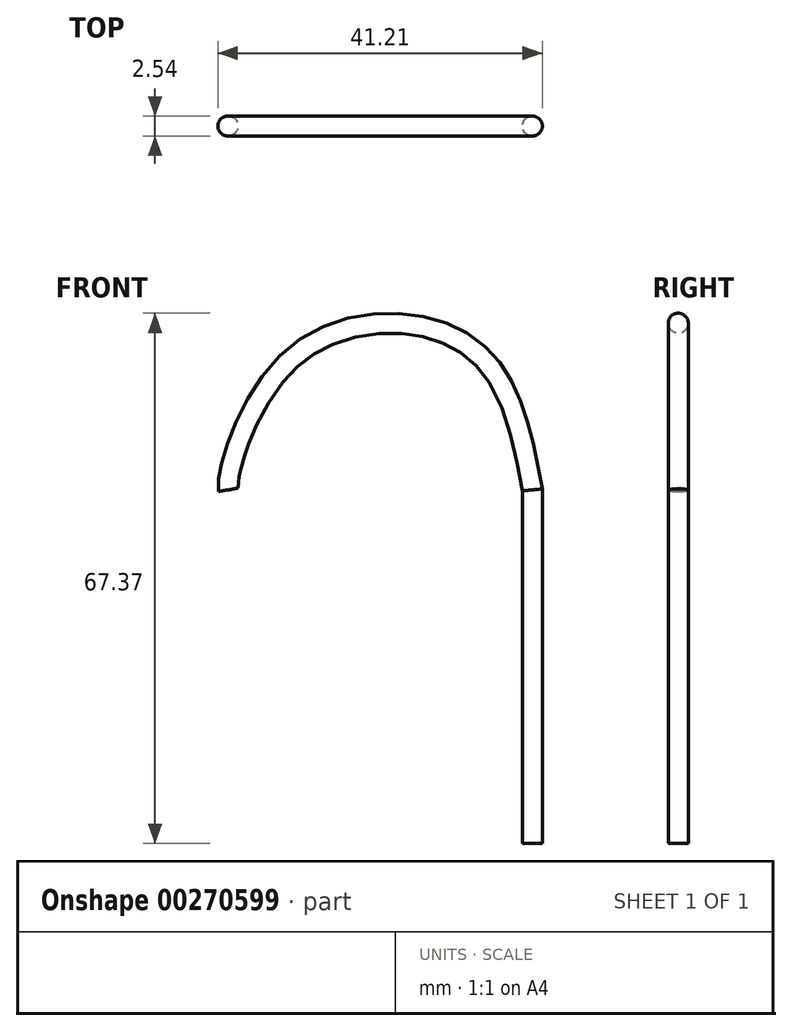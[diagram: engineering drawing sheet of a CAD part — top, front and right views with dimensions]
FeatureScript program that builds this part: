
annotation { "Feature Type Name" : "Feature", "Feature Type Description" : "" }
export const myFeature = defineFeature(function(context is Context, id is Id, definition is map)
    precondition{}
    {
        {
            var Q0;
            Q0=qCreatedBy(makeId("Top.planeOp"),FACE);
            var sketch = newSketch(context, id + "F0", { "sketchPlane" : qUnion([Q0])});
            skCircle(sketch, "E0", {"center": v(0, 0) * mm, "radius": 1.27 * mm});
            skSolve(sketch);
        }
        {
            var Q0;
            Q0=qCreatedBy(makeId("Front.planeOp"),FACE);
            var sketch = newSketch(context, id + "F1", { "sketchPlane" : qUnion([Q0])});
            skLineSegment(sketch, "E1", {"start": v(0, 0) * mm, "end": v(0, 44.92) * mm});
            skFitSpline(sketch, "E2", {"points": [v(0, 44.92) * mm, v(-8.11, 63.23) * mm, v(-30.42, 61.76) * mm, v(-38.64, 44.92) * mm], "startDerivative": vector(-12.2, 65.58) * mm, "endDerivative": vector(3.18, -17.96) * mm});
            skSolve(sketch);
        }
        {
            var Q0;
            Q0=makeQuery(id+"F0.imprint","IMPRINT",FACE,{"disambiguationData":[TD([[makeQuery(id+"F0.imprint","IMPRINT",EDGE,{"derivedFrom":sQuery(id+"F0.wireOp",EDGE,"E0")}),1.0]])]});
            var Q1;
            Q1=sQuery(id+"F1.wireOp",EDGE,"E1");
            var Q2;
            Q2=sQuery(id+"F1.wireOp",EDGE,"E2");
            sweep(context, id + "F2", {"profiles" : qUnion([Q0]), "path" : qUnion([Q1, Q2])});
        }
    });
